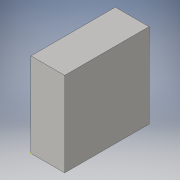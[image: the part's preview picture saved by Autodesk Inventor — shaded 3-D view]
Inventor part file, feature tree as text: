
AUTODESK INVENTOR PART (.ipt)
format: ipt  version: 2016 (Build 200138000, 138)  size: 83,968 bytes
history: native  units: in
note: dims shown in document units (in); Inventor stores cm internally (conversion verified against a paired STEP export)
features: sketch x2, extrude x1
ambient origin geometry x8: Origin, YZ Plane, XZ Plane, XY Plane, X Axis, Y Axis, Z Axis, Center Point
bodies: Solid1 (feature_tree)
feature tree (3):
  extrude  "Extrusion1"  Depth=1.9685in
  sketch  "Sketch2"  dims[d2=1.9685in d3=0.0in]
  sketch  "Sketch1"  dims[d0=0.7874in d1=1.9685in]
